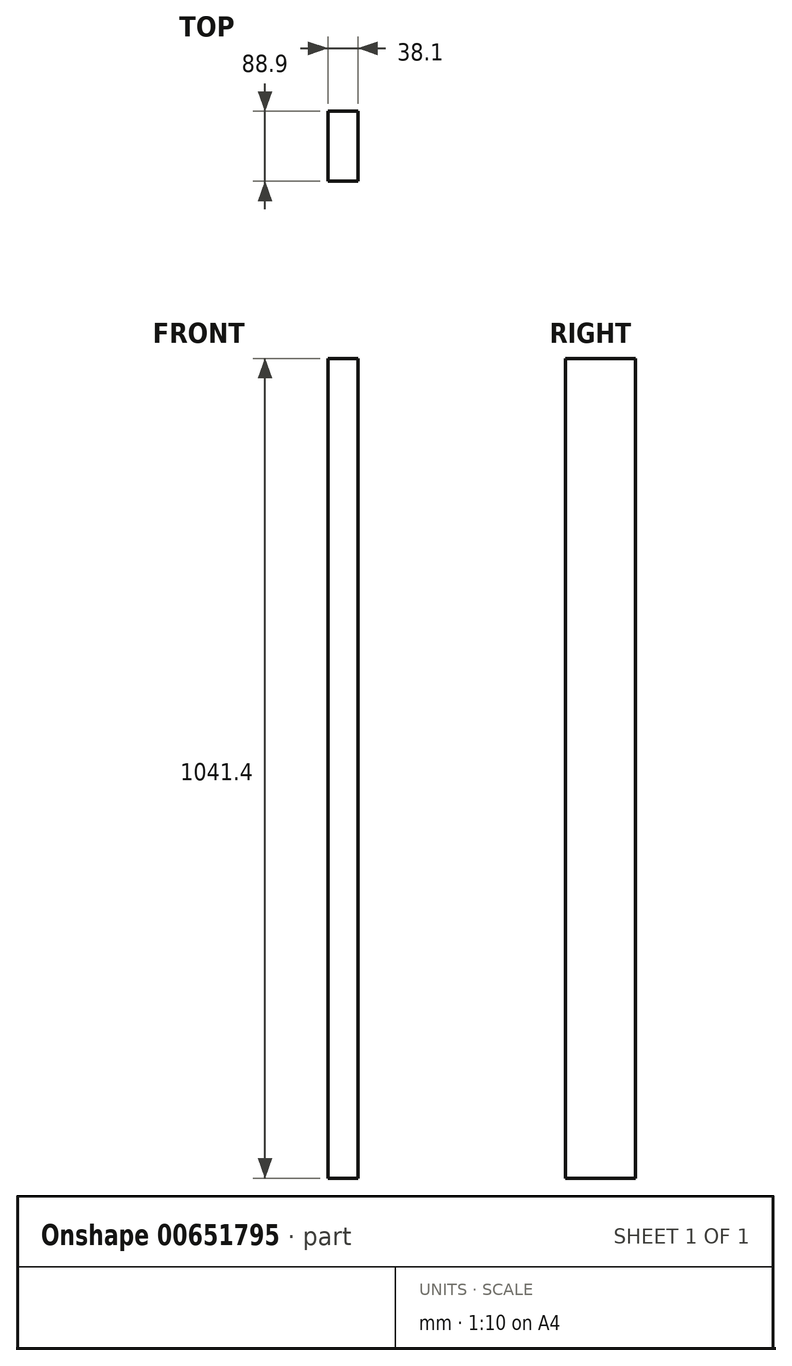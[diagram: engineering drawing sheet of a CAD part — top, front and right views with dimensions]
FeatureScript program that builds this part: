
annotation { "Feature Type Name" : "Feature", "Feature Type Description" : "" }
export const myFeature = defineFeature(function(context is Context, id is Id, definition is map)
    precondition{}
    {
        {
            var Q0;
            Q0=qCreatedBy(makeId("Top.planeOp"),FACE);
            var sketch = newSketch(context, id + "F0", { "sketchPlane" : qUnion([Q0])});
            skLineSegment(sketch, "E0.bottom", {"start": v(0, 0) * mm, "end": v(38.1, 0) * mm});
            skLineSegment(sketch, "E0.top", {"start": v(0, 88.9) * mm, "end": v(38.1, 88.9) * mm});
            skLineSegment(sketch, "E0.left", {"start": v(0, 0) * mm, "end": v(0, 88.9) * mm});
            skLineSegment(sketch, "E0.right", {"start": v(38.1, 0) * mm, "end": v(38.1, 88.9) * mm});
            skSolve(sketch);
        }
        {
            var Q0;
            Q0=makeQuery(id+"F0.imprint","IMPRINT",FACE,{"disambiguationData":[TD([[makeQuery(id+"F0.imprint","IMPRINT",EDGE,{"derivedFrom":sQuery(id+"F0.wireOp",EDGE,"E0.bottom")}),1.0]])]});
            extrude(context, id + "F1", {"entities" : qUnion([Q0]), "depth" : 1041.4 * mm, "offsetDistance" : 25.4 * mm});
        }
    });
